# Revit family: 4069216 Sylvania Lighting Fixture PATHE GROUND ROUND1 WIDE 69LM LED 4K
name_source: partatom
category: Lighting Fixtures
revit_build: Autodesk Revit 2016 (Build: 20150220_1215(x64)
units: mm (PartAtom-declared; Revit-internal decimal feet)

## family parameters
Cut with Voids When Loaded = No
Host = Face
Light Source = Yes
OmniClass Number = 23.80.70.00
OmniClass Title = Lighting
Part Type = Normal
Room Calculation Point = No
Round Connector Dimension = Use Diameter
Shared = No

## types (1)
- 4069216 PATHE/G/R1 WIDE 69LM LED 4K
    Apparent Load = 2 VA
    Assembly Code = D5020200
    AssetType = Fixed
    ChamferDiffuserSide_SYL = 1 mm  [stored 0.00328084 ft]
    ChamferDiffuserTop_SYL = 2 mm  [stored 0.00656168 ft]
    ChamferTop_SYL = 2 mm  [stored 0.00656168 ft]
    ClassificationName = Uniclass2015
    ClassificationValue = EF_70_80
    Color Filter = 16777215
    Cost = 0 $
    Default Elevation = 1219 mm
    Description = Round recessed ground luminaireCorrosion resistant die-cast aluminium, 69lm, 1.5W, 46lm/W, 4000K, CRI80+, 100°, non dimmable, IP68, IK10, (ØxD) Ø45x75mm, 3 step MacAdam ellipse, Class III, 12-24V-DC, A++ A+ A
    Dimming Lamp Color Temperature Shift = <None>
    DocumentationLiterature = http://www.sylvania-lighting.com
    DurationUnit = hours
    ElectricShockClassification = Class III
    Emit Shape Visible in Rendering = No
    Emit from Circle Diameter = 20 mm
    ExpectedLife = 50000
    HieghtTop_SYL = 2 mm  [stored 0.00656168 ft]
    IfcExportAs = IfcLightFixtureType
    IfcExportType = IfcLightFixtureType
    ImpactProtectionIndex = IK10
    IngressProtection = IP68
    Keynote = 16500
    Lamp = LED
    LampColourRenderingIndex = 80
    LampColourTemperature = 4000 K
    LampNominalLuminous = 69 lm
    LampsType = LED
    LightOutputRatio = 100
    LuminousEfficacy = 46 lm/W
    Manufacturer = Feilo Sylvania
    ManufacturerName = Feilo Sylvania
    Material = corrosion resistant die-cast aluminium housing, anti uv polycarbonate diffuser
    Material_1_SYL = Aluminum 6061 T6 80 Hot Formed
    Material_2_SYL = Polycarbonate, Clear
    Material_3_SYL = <By Category>
    Material_4_SYL = <By Category>
    Model = PATHE/GROUND/ROUND1 WIDE 69LM LED 4K
    ModelNumber = 4069216
    ModelReference = PATHE/GROUND/ROUND1 WIDE 69LM LED 4K
    Name = PATHE/GROUND/ROUND1 WIDE 69LM LED 4K
    NominalDepth = 0 mm  [stored 0 ft]
    NominalHeight = 75 mm
    NominalLength = 45 mm  [stored 0.147638 ft]
    Photometric Web File = 4069216.ies
    PowerConsumption = 1.5 W
    PowerFactor = 0
    RadiusDiffuser_SYL = 10 mm  [stored 0.0328084 ft]
    Radius_SYL = 23 mm
    Tilt Angle = -90.00°
    Type Image = <None>
    TypeName = PATHE/GROUND/ROUND1 WIDE 69LM LED 4K
    URL = http://www.sylvania-lighting.com
    Voltage = 0 V
    Weight = 0.23 kg

note: [stored X ft] marks values corroborated as IEEE doubles in the binary element streams (Revit-internal decimal feet)

## geometry (parser evidence)
native form markers: Sweep x3
no freeform markers — native parametric forms only
